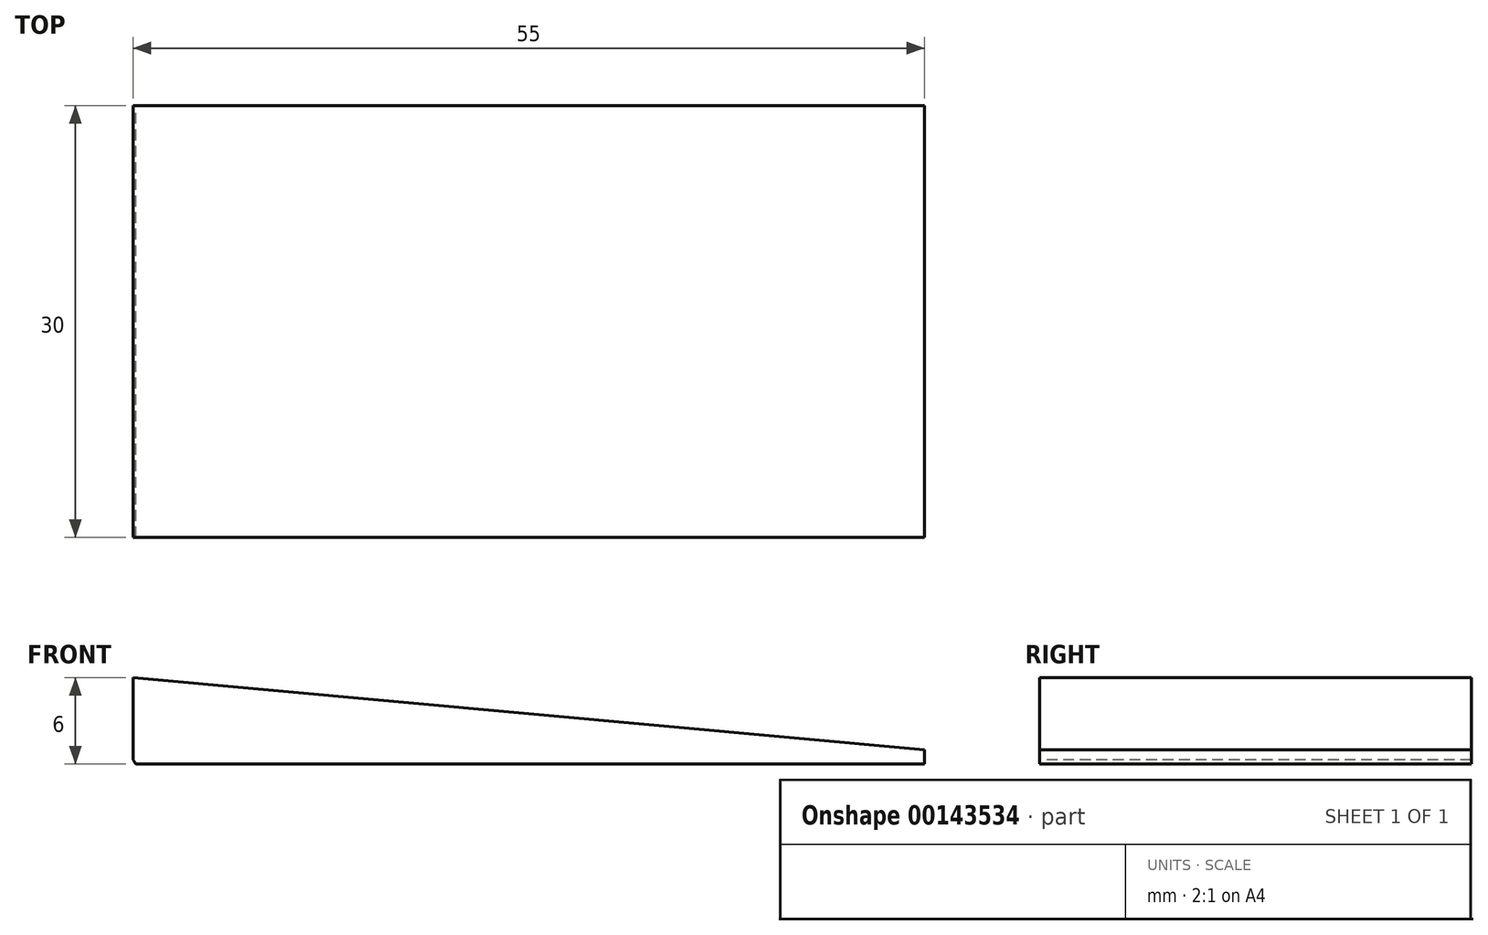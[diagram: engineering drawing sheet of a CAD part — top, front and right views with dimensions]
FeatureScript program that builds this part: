
annotation { "Feature Type Name" : "Feature", "Feature Type Description" : "" }
export const myFeature = defineFeature(function(context is Context, id is Id, definition is map)
    precondition{}
    {
        {
            var Q0;
            Q0=qCreatedBy(makeId("Front.planeOp"),FACE);
            var sketch = newSketch(context, id + "F0", { "sketchPlane" : qUnion([Q0])});
            skLineSegment(sketch, "E0", {"start": v(-27.5, 0) * mm, "end": v(-27.5, 6) * mm});
            skLineSegment(sketch, "E1", {"start": v(-27.5, 6) * mm, "end": v(27.5, 1) * mm});
            skLineSegment(sketch, "E2", {"start": v(27.5, 1) * mm, "end": v(27.5, 0) * mm});
            skLineSegment(sketch, "E3", {"start": v(27.5, 0) * mm, "end": v(-27.5, 0) * mm});
            skSolve(sketch);
        }
        {
            var Q0;
            Q0 = qSketchRegion(id + "F0", true);
            extrude(context, id + "F1", {"entities" : qUnion([Q0]), "depth" : 30 * mm});
        }
        {
            var Q0;
            Q0=makeQuery(id+"F1.opExtrude","SWEPT_EDGE",EDGE,{"disambiguationData":[OSD([sQuery(id+"F0.wireOp",EDGE,"E0"),sQuery(id+"F0.wireOp",EDGE,"E3")])]});
            chamfer(context, id + "F2", {"entities" : qUnion([Q0]), "chamferType" : ChamferType.TWO_OFFSETS, "width1" : .2 * mm, "oppositeDirection" : true, "width2" : .3 * mm, "tangentPropagation" : true});
        }
    });
